# Revit family: Cleanout-Round_Industrial_Floor-Zurn-Z1840-8B
name_source: partatom
category: Plumbing Fixtures
units: mm (PartAtom-declared; Revit-internal decimal feet)

## family parameters
Always vertical = Yes
Cut with Voids When Loaded = No
Maintain Annotation Orientation = No
OmniClass Number = 23.45.55.21
OmniClass Title = Drains (Wastes)
Part Type = Normal
Room Calculation Point = No
Round Connector Dimension = Use Radius
Shared = No
Work Plane-Based = No

## types (24) — shared parameters
Assembly Code = D2030300
CW Connection = No
Default Elevation = 20 "
Description = 8 INCH DIAMETER ROUND INDUSTRIAL FLOOR CLEANOUT
Drain Diameter = 8.625 "
Drain Radius = 4.313 "
Drain Total Height = 5.5 "
Grate Thickness = 0.563 "
HW Connection = No
Manufacturer = Zurn Water, LLC
Manufacurer Brand = Zurn
Modified Date = 01/30/26
Product Documentation Link = https://files.zurn.com
Product Page URL = https://www.zurn.com
Product data url = https://www.bimobject.com
URL = www.zurn.com
Vent Connection = No
WFU = 1
Waste Connection = Yes
zero-valued in all types: CWFU, HWFU

## per-type parameters (varying)
| type | Main Material | Model | Pipe Size 'A' (Inner Diameter) | Pipe Size 'A' (Inner Radius) | Pipe Size 'A' (Nominal Diameter) | Pipe Size 'A' (Nominal Radius) | Pipe Size 'A' (Outer Diameter) | Pipe Size 'A' (Outer Radius) | Type Comments |
| Z1840-8B-2BW | Steel - Zurn- Stainless - Type - 304 | Z1840-8B | 2.067 " | 1.034 " | 2 " | 1 " | 2.375 " | 1.188 " | Z1840-8B_2 Inch Butt-Weld Outlet with Floor Cleanout |
| Z1840-8B-3BW | Steel - Zurn- Stainless - Type - 304 | Z1840-8B | 3.068 " | 1.534 " | 3 " | 1.5 " | 3.5 " | 1.75 " | Z1840-8B_3 Inch Butt-Weld Outlet with Floor Cleanout |
| Z1840-8B-4BW | Steel - Zurn- Stainless - Type - 304 | Z1840-8B | 4.026 " | 2.013 " | 4 " | 2 " | 4.5 " | 2.25 " | Z1840-8B_4 Inch Butt-Weld Outlet with Floor Cleanout |
| Z1840-8B-6BW | Steel - Zurn- Stainless - Type - 304 | Z1840-8B | 6.065 " | 3.033 " | 6 " | 3 " | 6.625 " | 3.313 " | Z1840-8B_6 Inch Butt-Weld Outlet with Floor Cleanout |
| Z1840-8B-2NH | Steel - Zurn- Stainless - Type - 304 | Z1840-8B | 2.067 " | 1.034 " | 2 " | 1 " | 2.375 " | 1.188 " | Z1840-8B_2 Inch No-Hub Outlet with Floor Cleanout |
| Z1840-8B-3NH | Steel - Zurn- Stainless - Type - 304 | Z1840-8B | 3.068 " | 1.534 " | 3 " | 1.5 " | 3.5 " | 1.75 " | Z1840-8B_3 Inch No-Hub Outlet with Floor Cleanout |
| Z1840-8B-4NH | Steel - Zurn- Stainless - Type - 304 | Z1840-8B | 4.026 " | 2.013 " | 4 " | 2 " | 4.5 " | 2.25 " | Z1840-8B_4 Inch No-Hub Outlet with Floor Cleanout |
| Z1840-8B-6NH | Steel - Zurn- Stainless - Type - 304 | Z1840-8B | 6.065 " | 3.033 " | 6 " | 3 " | 6.625 " | 3.313 " | Z1840-8B_6 Inch No-Hub Outlet with Floor Cleanout |
| Z1840-8B-2A | Steel - Zurn- Stainless - Type - 304 | Z1840-8B | 2.067 " | 1.034 " | 2 " | 1 " | 2.375 " | 1.188 " | Z1840-8B_2 Inch Adjustable Threading Coupling Outlet with Floor Cleanout |
| Z1840-8B-3A | Steel - Zurn- Stainless - Type - 304 | Z1840-8B | 3.068 " | 1.534 " | 3 " | 1.5 " | 3.5 " | 1.75 " | Z1840-8B_3 Inch Adjustable Threading Coupling Outlet with Floor Cleanout |
| Z1840-8B-4A | Steel - Zurn- Stainless - Type - 304 | Z1840-8B | 4.026 " | 2.013 " | 4 " | 2 " | 4.5 " | 2.25 " | Z1840-8B_4 Inch Adjustable Threading Coupling Outlet with Floor Cleanout |
| Z1840-8B-6A | Steel - Zurn- Stainless - Type - 304 | Z1840-8B | 6.065 " | 3.033 " | 6 " | 3 " | 6.625 " | 3.313 " | Z1840-8B_6 Inch Adjustable Threading Coupling Outlet with Floor Cleanout |
| ZM1840-8B-2BW | Steel - Zurn- Stainless - Type - 316 | ZM1840-8B | 2.067 " | 1.034 " | 2 " | 1 " | 2.375 " | 1.188 " | ZM1840-8B_2 Inch Butt-Weld Outlet with Floor Cleanout |
| ZM1840-8B-3BW | Steel - Zurn- Stainless - Type - 316 | ZM1840-8B | 3.068 " | 1.534 " | 3 " | 1.5 " | 3.5 " | 1.75 " | ZM1840-8B_3 Inch Butt-Weld Outlet with Floor Cleanout |
| ZM1840-8B-4BW | Steel - Zurn- Stainless - Type - 316 | ZM1840-8B | 4.026 " | 2.013 " | 4 " | 2 " | 4.5 " | 2.25 " | ZM1840-8B_4 Inch Butt-Weld Outlet with Floor Cleanout |
| ZM1840-8B-6BW | Steel - Zurn- Stainless - Type - 316 | ZM1840-8B | 6.065 " | 3.033 " | 6 " | 3 " | 6.625 " | 3.313 " | ZM1840-8B_6 Inch Butt-Weld Outlet with Floor Cleanout |
| ZM1840-8B-2NH | Steel - Zurn- Stainless - Type - 316 | ZM1840-8B | 2.067 " | 1.034 " | 2 " | 1 " | 2.375 " | 1.188 " | ZM1840-8B_2 Inch No-Hub Outlet with Floor Cleanout |
| ZM1840-8B-3NH | Steel - Zurn- Stainless - Type - 316 | ZM1840-8B | 3.068 " | 1.534 " | 3 " | 1.5 " | 3.5 " | 1.75 " | ZM1840-8B_3 Inch No-Hub Outlet with Floor Cleanout |
| ZM1840-8B-4NH | Steel - Zurn- Stainless - Type - 316 | ZM1840-8B | 4.026 " | 2.013 " | 4 " | 2 " | 4.5 " | 2.25 " | ZM1840-8B_4 Inch No-Hub Outlet with Floor Cleanout |
| ZM1840-8B-6NH | Steel - Zurn- Stainless - Type - 316 | ZM1840-8B | 6.065 " | 3.033 " | 6 " | 3 " | 6.625 " | 3.313 " | ZM1840-8B_6 Inch No-Hub Outlet with Floor Cleanout |
| ZM1840-8B-2A | Steel - Zurn- Stainless - Type - 316 | ZM1840-8B | 2.067 " | 1.034 " | 2 " | 1 " | 2.375 " | 1.188 " | ZM1840-8B_2 Inch Adjustable Threading Coupling Outlet with Floor Cleanout |
| ZM1840-8B-3A | Steel - Zurn- Stainless - Type - 316 | ZM1840-8B | 3.068 " | 1.534 " | 3 " | 1.5 " | 3.5 " | 1.75 " | ZM1840-8B_3 Inch Adjustable Threading Coupling Outlet with Floor Cleanout |
| ZM1840-8B-4A | Steel - Zurn- Stainless - Type - 316 | ZM1840-8B | 4.026 " | 2.013 " | 4 " | 2 " | 4.5 " | 2.25 " | ZM1840-8B_4 Inch Adjustable Threading Coupling Outlet with Floor Cleanout |
| ZM1840-8B-6A | Steel - Zurn- Stainless - Type - 316 | ZM1840-8B | 6.065 " | 3.033 " | 6 " | 3 " | 6.625 " | 3.313 " | ZM1840-8B_6 Inch Adjustable Threading Coupling Outlet with Floor Cleanout |

## geometry (parser evidence)
native form markers: Sweep x2
no freeform markers — native parametric forms only
